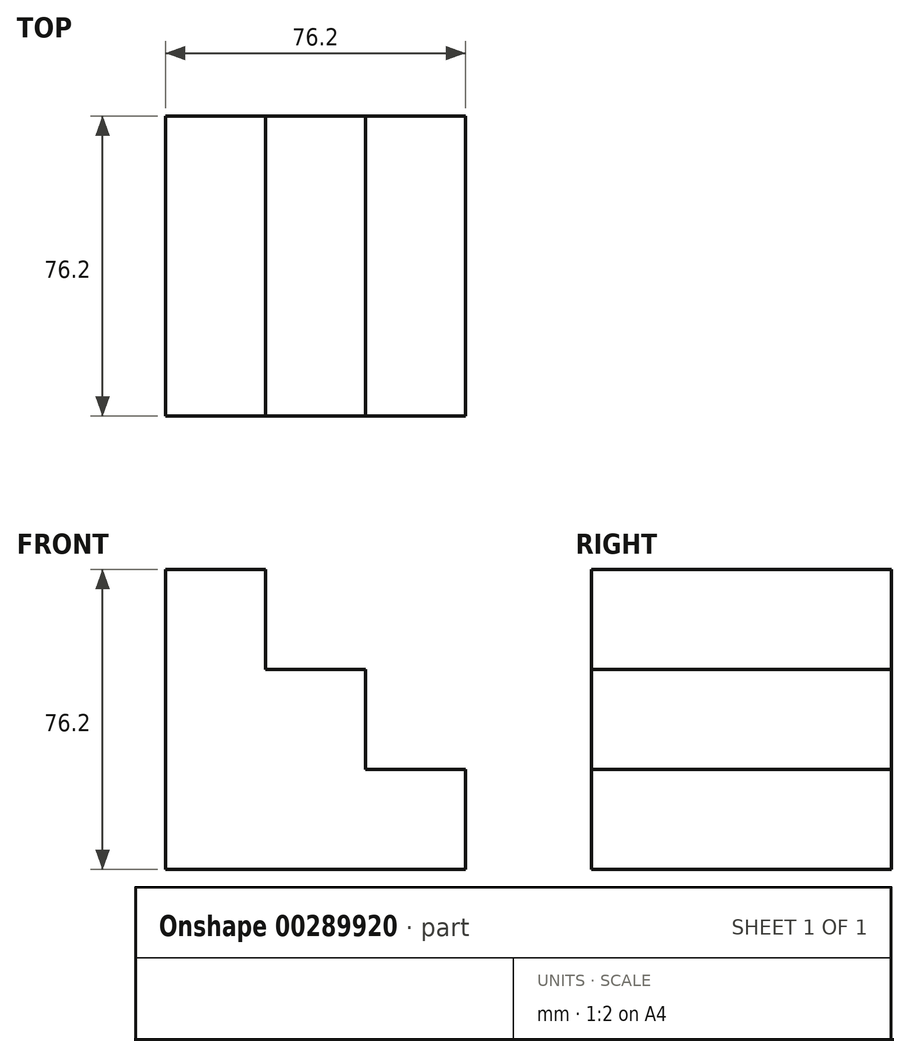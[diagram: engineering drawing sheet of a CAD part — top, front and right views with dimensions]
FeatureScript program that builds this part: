
annotation { "Feature Type Name" : "Feature", "Feature Type Description" : "" }
export const myFeature = defineFeature(function(context is Context, id is Id, definition is map)
    precondition{}
    {
        {
            var Q0;
            Q0=qCreatedBy(makeId("Front.planeOp"),FACE);
            var sketch = newSketch(context, id + "F0", { "sketchPlane" : qUnion([Q0])});
            skLineSegment(sketch, "E0", {"start": v(0, 0) * mm, "end": v(-76.2, 0) * mm});
            skLineSegment(sketch, "E1", {"start": v(-76.2, 0) * mm, "end": v(-76.2, 76.2) * mm});
            skLineSegment(sketch, "E2", {"start": v(-76.2, 76.2) * mm, "end": v(-50.8, 76.2) * mm});
            skLineSegment(sketch, "E3", {"start": v(-50.8, 76.2) * mm, "end": v(-50.8, 50.8) * mm});
            skLineSegment(sketch, "E4", {"start": v(-50.8, 50.8) * mm, "end": v(-25.4, 50.8) * mm});
            skLineSegment(sketch, "E5", {"start": v(-25.4, 50.8) * mm, "end": v(-25.4, 25.4) * mm});
            skLineSegment(sketch, "E6", {"start": v(-25.4, 25.4) * mm, "end": v(0, 25.4) * mm});
            skLineSegment(sketch, "E7", {"start": v(0, 25.4) * mm, "end": v(0, 0) * mm});
            skSolve(sketch);
        }
        {
            var Q0;
            Q0=makeQuery(id+"F0.imprint","IMPRINT",FACE,{"disambiguationData":[TD([[makeQuery(id+"F0.imprint","IMPRINT",EDGE,{"derivedFrom":sQuery(id+"F0.wireOp",EDGE,"E0")}),-1.0]])]});
            extrude(context, id + "F1", {"entities" : qUnion([Q0]), "depth" : 76.2 * mm});
        }
    });
